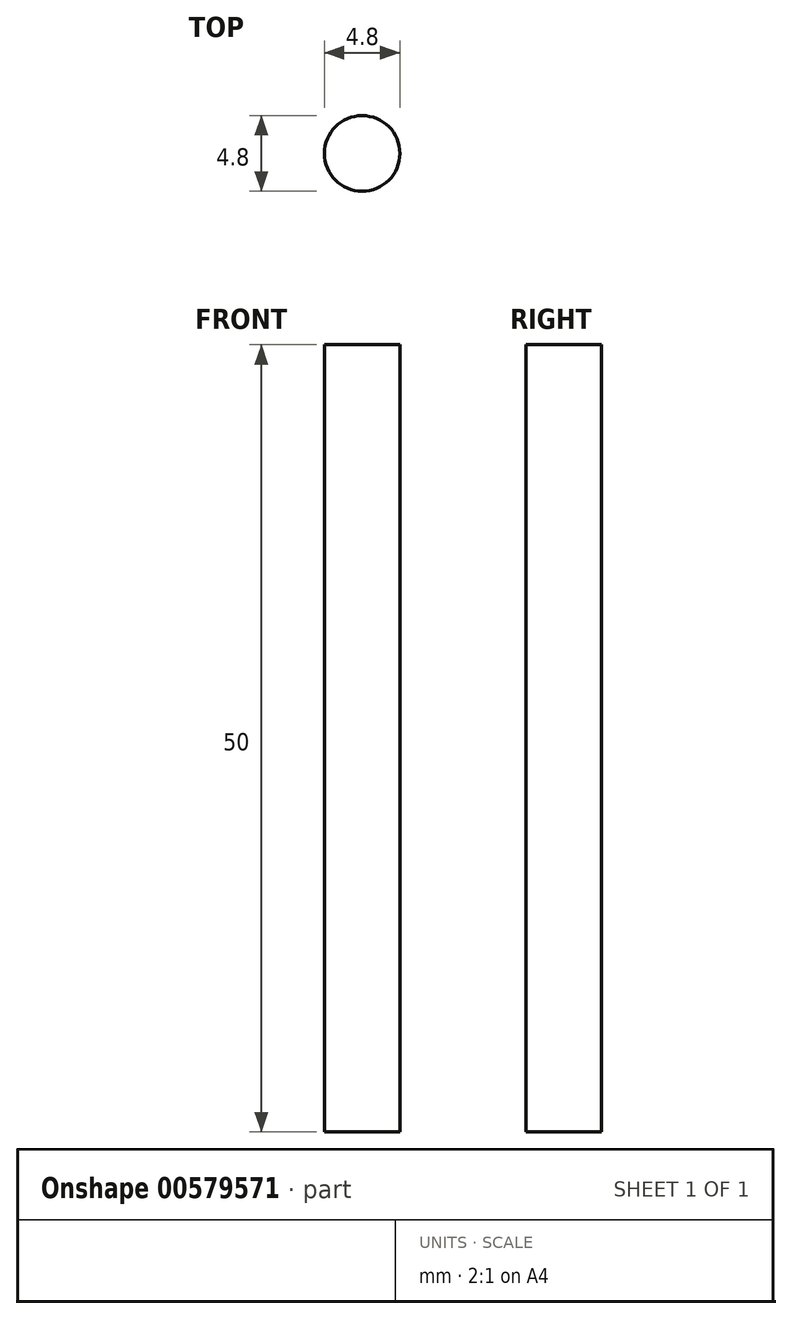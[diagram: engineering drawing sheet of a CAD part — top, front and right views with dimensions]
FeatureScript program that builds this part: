
annotation { "Feature Type Name" : "Feature", "Feature Type Description" : "" }
export const myFeature = defineFeature(function(context is Context, id is Id, definition is map)
    precondition{}
    {
        {
            var Q0;
            Q0=qCreatedBy(makeId("Top.planeOp"),FACE);
            var sketch = newSketch(context, id + "F0", { "sketchPlane" : qUnion([Q0])});
            skCircle(sketch, "E0", {"center": v(0, 0) * mm, "radius": 2.4 * mm});
            skSolve(sketch);
        }
        {
            var Q0;
            Q0=makeQuery(id+"F0.imprint","IMPRINT",FACE,{"disambiguationData":[TD([[makeQuery(id+"F0.imprint","IMPRINT",EDGE,{"derivedFrom":sQuery(id+"F0.wireOp",EDGE,"E0")}),1.0]])]});
            extrude(context, id + "F1", {"entities" : qUnion([Q0]), "depth" : 50 * mm, "offsetDistance" : 25 * mm});
        }
    });
